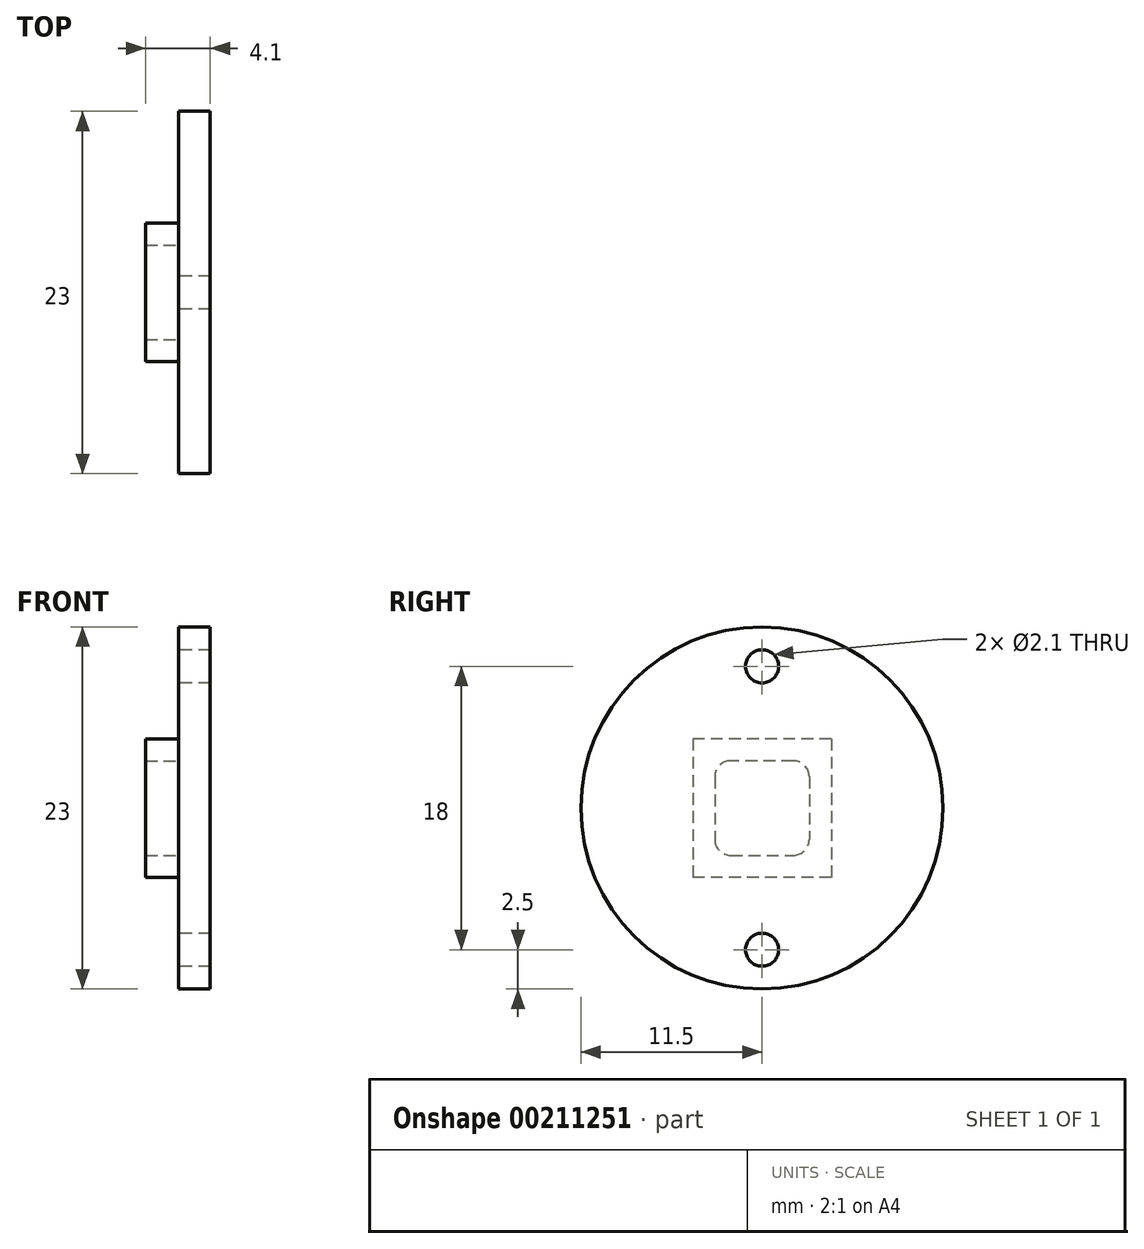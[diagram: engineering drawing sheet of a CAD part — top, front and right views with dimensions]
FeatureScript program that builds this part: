
annotation { "Feature Type Name" : "Feature", "Feature Type Description" : "" }
export const myFeature = defineFeature(function(context is Context, id is Id, definition is map)
    precondition{}
    {
        {
            var Q0;
            Q0=qCreatedBy(makeId("Right.planeOp"),FACE);
            var sketch = newSketch(context, id + "F0", { "sketchPlane" : qUnion([Q0])});
            skCircle(sketch, "E0", {"center": v(0, 0) * mm, "radius": 11.5 * mm});
            skCircle(sketch, "E1", {"center": v(0, 0) * mm, "radius": 9 * mm, "construction": true});
            skCircle(sketch, "E2", {"center": v(0, 9) * mm, "radius": 1.05 * mm});
            skCircle(sketch, "E3", {"center": v(0, -9) * mm, "radius": 1.05 * mm});
            skSolve(sketch);
        }
        {
            var Q0;
            Q0=qSketchRegion(id+"F0",true);
            extrude(context, id + "F1", {"entities" : qUnion([Q0]), "depth" : 2 * mm});
        }
        {
            var Q0;
            Q0=makeQuery(id+"F1.opExtrude","CAP_FACE",FACE,{"disambiguationData":[OSD([sQuery(id+"F0.wireOp",EDGE,"E0"),sQuery(id+"F0.wireOp",EDGE,"E2"),sQuery(id+"F0.wireOp",EDGE,"E3")])],"isStart":true});
            var sketch = newSketch(context, id + "F2", { "sketchPlane" : qUnion([Q0])});
            skLineSegment(sketch, "E4.bottom", {"start": v(-4.4, 4.4) * mm, "end": v(4.4, 4.4) * mm});
            skLineSegment(sketch, "E4.top", {"start": v(-4.4, -4.4) * mm, "end": v(4.4, -4.4) * mm});
            skLineSegment(sketch, "E4.left", {"start": v(-4.4, 4.4) * mm, "end": v(-4.4, -4.4) * mm});
            skLineSegment(sketch, "E4.right", {"start": v(4.4, 4.4) * mm, "end": v(4.4, -4.4) * mm});
            skPoint(sketch, "E5.middle", {"position": v(0, 0) * mm});
            skArc(sketch, "E6", {"start": v(-2, 3) * mm, "mid": v(-2.7, 2.7) * mm, "end": v(-3, 2) * mm});
            skArc(sketch, "E7", {"start": v(-3, -2) * mm, "mid": v(-2.7, -2.7) * mm, "end": v(-2, -3) * mm});
            skArc(sketch, "E8", {"start": v(2, -3) * mm, "mid": v(2.7, -2.7) * mm, "end": v(3, -2) * mm});
            skArc(sketch, "E9", {"start": v(3, 2) * mm, "mid": v(2.7, 2.7) * mm, "end": v(2, 3) * mm});
            skLineSegment(sketch, "E10", {"start": v(-2, 3) * mm, "end": v(2, 3) * mm});
            skLineSegment(sketch, "E11", {"start": v(3, 2) * mm, "end": v(3, -2) * mm});
            skLineSegment(sketch, "E12", {"start": v(2, -3) * mm, "end": v(-2, -3) * mm});
            skLineSegment(sketch, "E13", {"start": v(-3, 2) * mm, "end": v(-3, -2) * mm});
            skSolve(sketch);
        }
        {
            var Q0;
            Q0=qSketchRegion(id+"F2",true);
            extrude(context, id + "F3", {"entities" : qUnion([Q0]), "operationType" : NewBodyOperationType.ADD, "offsetDistance" : 25 * mm, "depth" : 2.1 * mm});
        }
    });
